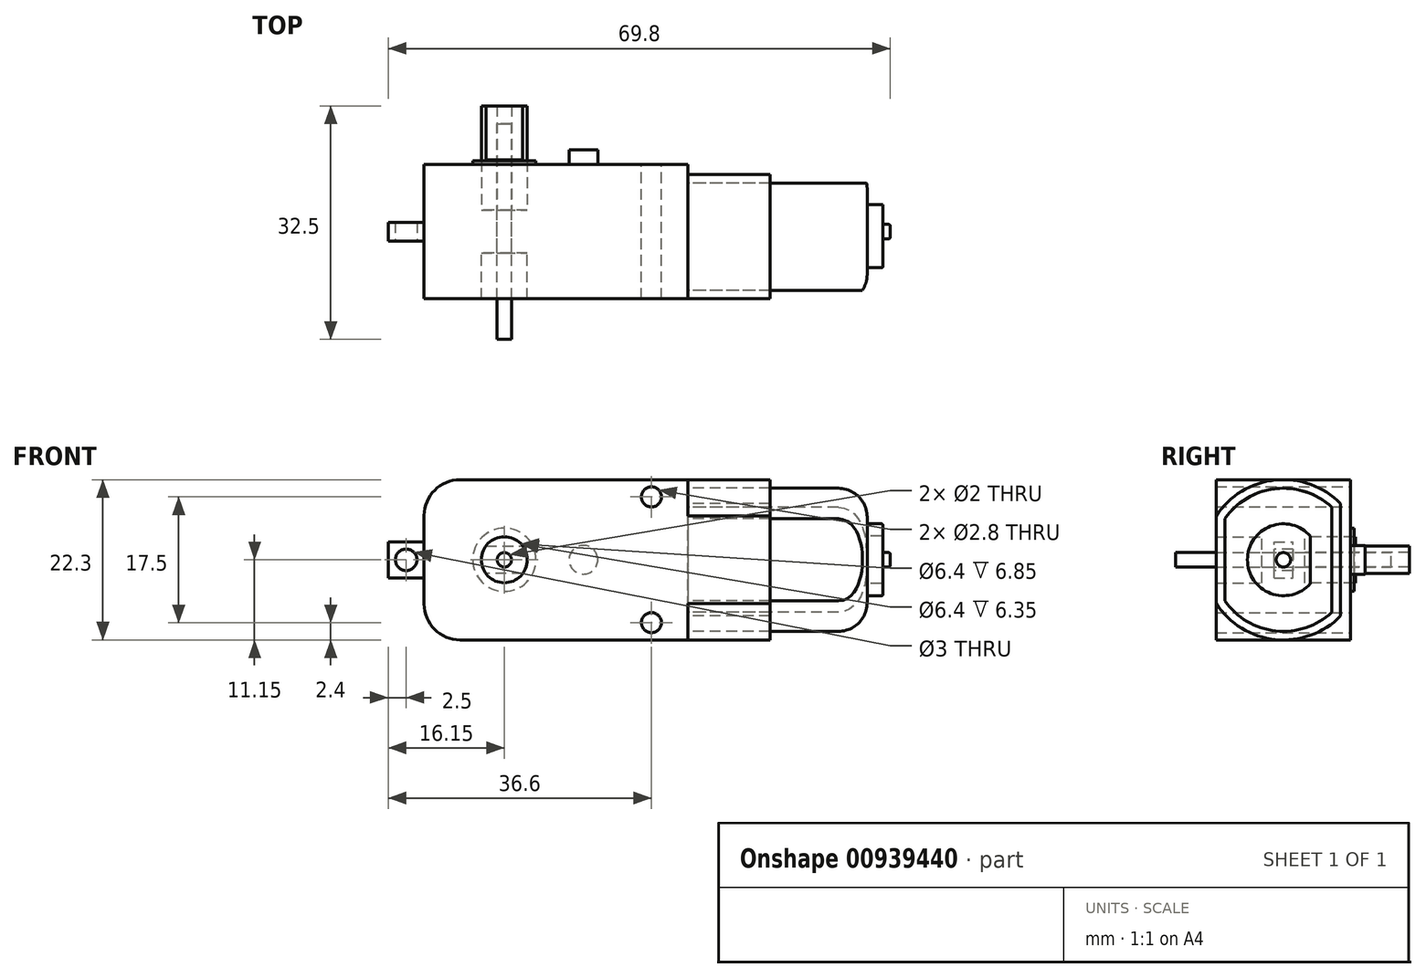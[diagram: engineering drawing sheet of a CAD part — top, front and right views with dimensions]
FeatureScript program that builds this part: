
annotation { "Feature Type Name" : "Feature", "Feature Type Description" : "" }
export const myFeature = defineFeature(function(context is Context, id is Id, definition is map)
    precondition{}
    {
        {
            var Q0;
            Q0=qCreatedBy(makeId("Front.planeOp"),FACE);
            var sketch = newSketch(context, id + "F0", { "sketchPlane" : qUnion([Q0])});
            skLineSegment(sketch, "E0.bottom", {"start": v(18.35, -11.15) * mm, "end": v(-13.35, -11.15) * mm});
            skLineSegment(sketch, "E0.top", {"start": v(18.35, 11.15) * mm, "end": v(-13.35, 11.15) * mm});
            skLineSegment(sketch, "E0.left", {"start": v(18.35, -11.15) * mm, "end": v(18.35, 11.15) * mm});
            skLineSegment(sketch, "E0.right", {"start": v(-18.35, -6.15) * mm, "end": v(-18.35, 6.15) * mm});
            skPoint(sketch, "E0.middle", {"position": v(0, 0) * mm});
            skPoint(sketch, "E1.visualSharp", {"position": v(-18.35, 11.15) * mm});
            skArc(sketch, "E1.filletArc", {"start": v(-13.35, 11.15) * mm, "mid": v(-16.89, 9.69) * mm, "end": v(-18.35, 6.15) * mm});
            skPoint(sketch, "E2.visualSharp", {"position": v(-18.35, -11.15) * mm});
            skArc(sketch, "E2.filletArc", {"start": v(-18.35, -6.15) * mm, "mid": v(-16.89, -9.69) * mm, "end": v(-13.35, -11.15) * mm});
            skLineSegment(sketch, "E3", {"start": v(-27.57, 10.15) * mm, "end": v(27, 10.15) * mm, "construction": true});
            skLineSegment(sketch, "E4", {"start": v(27, -10.15) * mm, "end": v(-33.16, -10.15) * mm, "construction": true});
            skLineSegment(sketch, "E5", {"start": v(14.65, 15.01) * mm, "end": v(14.65, -22.1) * mm, "construction": true});
            skCircle(sketch, "E6", {"center": v(13.25, 8.75) * mm, "radius": 1.4 * mm});
            skCircle(sketch, "E7.MirrorC", {"center": v(13.25, -8.75) * mm, "radius": 1.4 * mm});
            skCircle(sketch, "E8", {"center": v(-7.2, 0) * mm, "radius": 3.2 * mm});
            skCircle(sketch, "E9", {"center": v(-7.2, 0) * mm, "radius": 1 * mm});
            skCircle(sketch, "E10", {"center": v(3.8, 0) * mm, "radius": 2 * mm});
            skSolve(sketch);
        }
        {
            var Q0;
            Q0=makeQuery(id+"F0.imprint","IMPRINT",FACE,{"disambiguationData":[TD([[makeQuery(id+"F0.imprint","IMPRINT",EDGE,{"derivedFrom":sQuery(id+"F0.wireOp",EDGE,"E0.bottom")}),-1.0]])]});
            var Q1;
            Q1=makeQuery(id+"F0.imprint","IMPRINT",FACE,{"disambiguationData":[TD([[makeQuery(id+"F0.imprint","IMPRINT",EDGE,{"derivedFrom":sQuery(id+"F0.wireOp",EDGE,"E10")}),1.0]])]});
            extrude(context, id + "F1", {"entities" : qUnion([Q0, Q1]), "endBound" : BoundingType.SYMMETRIC, "offsetDistance" : 25 * mm, "depth" : (18.7) * mm});
        }
        {
            var Q0;
            Q0=makeQuery(id+"F0.imprint","IMPRINT",FACE,{"disambiguationData":[TD([[makeQuery(id+"F0.imprint","IMPRINT",EDGE,{"derivedFrom":sQuery(id+"F0.wireOp",EDGE,"E10")}),1.0]])]});
            var Q1;
            Q1=sQuery(id+"F0.wireOp",EDGE,"E10");
            extrude(context, id + "F2", {"entities" : qUnion([Q0]), "operationType" : NewBodyOperationType.ADD, "surfaceEntities" : qUnion([Q1]), "oppositeDirection" : true, "depth" : 11.35 * mm, "offsetDistance" : 25 * mm});
        }
        {
            var Q0;
            Q0=makeQuery(id+"F1.opExtrude","SWEPT_FACE",FACE,{"disambiguationData":[OSD([sQuery(id+"F0.wireOp",EDGE,"E0.right")])]});
            var sketch = newSketch(context, id + "F3", { "sketchPlane" : qUnion([Q0])});
            skLineSegment(sketch, "E11.bottom", {"start": v(1.3, -2.5) * mm, "end": v(-1.3, -2.5) * mm});
            skLineSegment(sketch, "E11.top", {"start": v(1.3, 2.5) * mm, "end": v(-1.3, 2.5) * mm});
            skLineSegment(sketch, "E11.left", {"start": v(1.3, -2.5) * mm, "end": v(1.3, 2.5) * mm});
            skLineSegment(sketch, "E11.right", {"start": v(-1.3, -2.5) * mm, "end": v(-1.3, 2.5) * mm});
            skPoint(sketch, "E11.middle", {"position": v(0, 0) * mm});
            skSolve(sketch);
        }
        {
            var Q0;
            Q0=makeQuery(id+"F3.imprint","IMPRINT",FACE,{"disambiguationData":[TD([[makeQuery(id+"F3.imprint","IMPRINT",EDGE,{"derivedFrom":sQuery(id+"F3.wireOp",EDGE,"E11.bottom")}),-1.0]])]});
            extrude(context, id + "F4", {"entities" : qUnion([Q0]), "operationType" : NewBodyOperationType.ADD, "depth" : 5 * mm});
        }
        {
            var Q0;
            Q0=makeQuery(id+"F4.opExtrude","SWEPT_FACE",FACE,{"disambiguationData":[OSD([sQuery(id+"F3.wireOp",EDGE,"E11.left")])]});
            var sketch = newSketch(context, id + "F5", { "sketchPlane" : qUnion([Q0])});
            skLineSegment(sketch, "E12", {"start": v(-23.35, 0) * mm, "end": v(-18.35, 0) * mm, "construction": true});
            skCircle(sketch, "E13", {"center": v(-20.85, 0) * mm, "radius": 1.5 * mm});
            skSolve(sketch);
        }
        {
            var Q0;
            Q0=makeQuery(id+"F5.imprint","IMPRINT",FACE,{"disambiguationData":[TD([[makeQuery(id+"F5.imprint","IMPRINT",EDGE,{"derivedFrom":sQuery(id+"F5.wireOp",EDGE,"E13")}),1.0]])]});
            extrude(context, id + "F6", {"entities" : qUnion([Q0]), "operationType" : NewBodyOperationType.REMOVE, "endBound" : BoundingType.THROUGH_ALL, "oppositeDirection" : true, "depth" : 25 * mm});
        }
        {
            var Q0;
            Q0=makeQuery(id+"F1.opExtrude","SWEPT_FACE",FACE,{"disambiguationData":[OSD([sQuery(id+"F0.wireOp",EDGE,"E0.left")])]});
            var sketch = newSketch(context, id + "F7", { "sketchPlane" : qUnion([Q0])});
            skArc(sketch, "E14", {"start": v(7.95, 7.82) * mm, "mid": v(-1.12, 11.1) * mm, "end": v(-9.35, 6.07) * mm});
            skLineSegment(sketch, "E15", {"start": v(7.95, 13.91) * mm, "end": v(7.95, -13.85) * mm, "construction": true});
            skLineSegment(sketch, "E16", {"start": v(-9.35, 11.15) * mm, "end": v(-9.35, -11.15) * mm, "construction": true});
            skArc(sketch, "E17.trimOffspring", {"start": v(-9.35, -6.07) * mm, "mid": v(-1.12, -11.1) * mm, "end": v(7.95, -7.82) * mm});
            skLineSegment(sketch, "E18", {"start": v(-9.35, 6.07) * mm, "end": v(-9.35, -6.07) * mm});
            skLineSegment(sketch, "E19", {"start": v(7.95, 7.82) * mm, "end": v(7.95, -7.82) * mm});
            skArc(sketch, "E20.0", {"start": v(-8.15, -5.7) * mm, "mid": v(-1.06, -9.9) * mm, "end": v(6.75, -7.31) * mm});
            skLineSegment(sketch, "E20.1", {"start": v(-8.15, 5.7) * mm, "end": v(-8.15, -5.7) * mm});
            skArc(sketch, "E20.2", {"start": v(6.75, 7.31) * mm, "mid": v(-1.06, 9.9) * mm, "end": v(-8.15, 5.7) * mm});
            skLineSegment(sketch, "E20.3", {"start": v(6.75, 7.31) * mm, "end": v(6.75, -7.31) * mm});
            skSolve(sketch);
        }
        {
            var Q0;
            {var subQ4=sQuery(id+"F7.wireOp",EDGE,"E18");Q0=makeQuery(id+"F7.imprint","IMPRINT",FACE,{"disambiguationData":[TD([[makeQuery(id+"F7.imprint","IMPRINT",EDGE,{"derivedFrom":subQ4}),-1.0]])]});}
            extrude(context, id + "F8", {"entities" : qUnion([Q0]), "operationType" : NewBodyOperationType.ADD, "depth" : 11.4 * mm});
        }
        {
            var Q0;
            Q0=makeQuery(id+"F8.boolean.opBoolean","SPLIT",FACE,{"disambiguationData":[TD([makeQuery(id+"F8.opExtrude","SWEPT_FACE",FACE,{"disambiguationData":[OSD([sQuery(id+"F7.wireOp",EDGE,"E20.0")])]}),makeQuery(id+"F8.opExtrude","SWEPT_FACE",FACE,{"disambiguationData":[OSD([sQuery(id+"F7.wireOp",EDGE,"E20.1")])]}),makeQuery(id+"F8.opExtrude","SWEPT_FACE",FACE,{"disambiguationData":[OSD([sQuery(id+"F7.wireOp",EDGE,"E20.2")])]}),makeQuery(id+"F8.opExtrude","SWEPT_FACE",FACE,{"disambiguationData":[OSD([sQuery(id+"F7.wireOp",EDGE,"E20.3")])]})])],"derivedFrom":makeQuery(id+"F1.opExtrude","SWEPT_FACE",FACE,{"disambiguationData":[OSD([sQuery(id+"F0.wireOp",EDGE,"E0.left")])]})});
            extrude(context, id + "F9", {"entities" : qUnion([Q0]), "depth" : (11.4 + 13.5) * mm});
        }
        {
            var Q0;
            Q0=makeQuery(id+"F9.opExtrude","CAP_EDGE",EDGE,{"disambiguationData":[OSD([sQuery(id+"F7.wireOp",EDGE,"E20.0")])],"isStart":false});
            fillet(context, id + "F10", {"entities" : qUnion([Q0]), "radius" : 4 * mm, "tangentPropagation" : true, "allowEdgeOverflow" : false});
        }
        {
            var Q0;
            Q0=makeQuery(id+"F9.opExtrude","CAP_FACE",FACE,{"disambiguationData":[OSD([sQuery(id+"F0.wireOp",EDGE,"E0.left")])],"isStart":false});
            var sketch = newSketch(context, id + "F11", { "sketchPlane" : qUnion([Q0])});
            skLineSegment(sketch, "E21", {"start": v(3.75, -5.9) * mm, "end": v(3.75, 7.54) * mm, "construction": true});
            skArc(sketch, "E22", {"start": v(3.75, 3.3) * mm, "mid": v(-5, 0) * mm, "end": v(3.75, -3.3) * mm});
            skLineSegment(sketch, "E23", {"start": v(3.75, 3.3) * mm, "end": v(3.75, -3.3) * mm});
            skCircle(sketch, "E24", {"center": v(0, 0) * mm, "radius": 1 * mm});
            skSolve(sketch);
        }
        {
            var Q0;
            Q0=makeQuery(id+"F0.imprint","IMPRINT",FACE,{"disambiguationData":[TD([[makeQuery(id+"F0.imprint","IMPRINT",EDGE,{"derivedFrom":sQuery(id+"F0.wireOp",EDGE,"E8")}),1.0]])]});
            extrude(context, id + "F12", {"entities" : qUnion([Q0]), "operationType" : NewBodyOperationType.ADD, "endBound" : BoundingType.SYMMETRIC, "depth" : 6 * mm});
        }
        {
            var Q0;
            Q0=makeQuery(id+"F0.imprint","IMPRINT",FACE,{"disambiguationData":[TD([[makeQuery(id+"F0.imprint","IMPRINT",EDGE,{"derivedFrom":sQuery(id+"F0.wireOp",EDGE,"E9")}),1.0]])]});
            extrude(context, id + "F13", {"entities" : qUnion([Q0]), "endBound" : BoundingType.SYMMETRIC, "depth" : 30 * mm});
        }
        {
            var Q0;
            Q0=makeQuery(id+"F1.opExtrude","CAP_FACE",FACE,{"disambiguationData":[OSD([sQuery(id+"F0.wireOp",EDGE,"E0.bottom"),sQuery(id+"F0.wireOp",EDGE,"E0.top"),sQuery(id+"F0.wireOp",EDGE,"E0.left"),sQuery(id+"F0.wireOp",EDGE,"E0.right"),sQuery(id+"F0.wireOp",EDGE,"E1.filletArc"),sQuery(id+"F0.wireOp",EDGE,"E2.filletArc"),sQuery(id+"F0.wireOp",EDGE,"E6"),sQuery(id+"F0.wireOp",EDGE,"E7.MirrorC"),sQuery(id+"F0.wireOp",EDGE,"E8")])],"isStart":true});
            var sketch = newSketch(context, id + "F14", { "sketchPlane" : qUnion([Q0])});
            skCircle(sketch, "E25", {"center": v(7.2, 0) * mm, "radius": 3.2 * mm});
            skCircle(sketch, "E26.0", {"center": v(7.2, 0) * mm, "radius": 4.4 * mm});
            skSolve(sketch);
        }
        {
            var Q0;
            Q0=makeQuery(id+"F14.imprint","IMPRINT",FACE,{"disambiguationData":[TD([[makeQuery(id+"F14.imprint","IMPRINT",EDGE,{"derivedFrom":sQuery(id+"F14.wireOp",EDGE,"E25")}),1.0]])]});
            extrude(context, id + "F15", {"entities" : qUnion([Q0]), "operationType" : NewBodyOperationType.ADD, "depth" : .5 * mm});
        }
        {
            var Q0;
            Q0=makeQuery(id+"F12.opExtrude","CAP_FACE",FACE,{"disambiguationData":[OSD([sQuery(id+"F0.wireOp",EDGE,"E8"),sQuery(id+"F0.wireOp",EDGE,"E9")])],"isStart":true});
            var sketch = newSketch(context, id + "F16", { "sketchPlane" : qUnion([Q0])});
            skCircle(sketch, "E27", {"center": v(7.2, 0) * mm, "radius": 1 * mm});
            skCircle(sketch, "E28", {"center": v(7.2, 0) * mm, "radius": 3.2 * mm});
            skSolve(sketch);
        }
        {
            var Q0;
            Q0=makeQuery(id+"F16.imprint","IMPRINT",FACE,{"disambiguationData":[TD([[makeQuery(id+"F16.imprint","IMPRINT",EDGE,{"derivedFrom":sQuery(id+"F16.wireOp",EDGE,"E27")}),1.0]])]});
            extrude(context, id + "F17", {"entities" : qUnion([Q0]), "depth" : 14.5 * mm});
        }
        {
            var Q0;
            Q0=makeQuery(id+"F17.opExtrude","CAP_FACE",FACE,{"disambiguationData":[OSD([sQuery(id+"F16.wireOp",EDGE,"E27"),sQuery(id+"F16.wireOp",EDGE,"E28")])],"isStart":false});
            var sketch = newSketch(context, id + "F18", { "sketchPlane" : qUnion([Q0])});
            skLineSegment(sketch, "E29", {"start": v(13.52, -1.92) * mm, "end": v(0.5, -1.92) * mm, "construction": true});
            skLineSegment(sketch, "E30", {"start": v(0.5, -1.92) * mm, "end": v(0.83, 1.03) * mm, "construction": true});
            skLineSegment(sketch, "E31.MirrorCS", {"start": v(13.52, 1.92) * mm, "end": v(0.5, 1.92) * mm, "construction": true});
            skLineSegment(sketch, "E32", {"start": v(9.76, 1.92) * mm, "end": v(4.64, 1.92) * mm});
            skLineSegment(sketch, "E33", {"start": v(4.64, -1.92) * mm, "end": v(9.76, -1.92) * mm});
            skSolve(sketch);
        }
        {
            var Q0;
            {var subQ0=sQuery(id+"F18.wireOp",EDGE,"E32");Q0=makeQuery(id+"F18.imprint","IMPRINT",FACE,{"disambiguationData":[TD([[makeQuery(id+"F18.imprint","IMPRINT",EDGE,{"derivedFrom":subQ0}),-1.0]])]});}
            var Q1;
            {var subQ0=sQuery(id+"F18.wireOp",EDGE,"E33");Q1=makeQuery(id+"F18.imprint","IMPRINT",FACE,{"disambiguationData":[TD([[makeQuery(id+"F18.imprint","IMPRINT",EDGE,{"derivedFrom":subQ0}),-1.0]])]});}
            extrude(context, id + "F19", {"entities" : qUnion([Q0, Q1]), "operationType" : NewBodyOperationType.REMOVE, "oppositeDirection" : true, "depth" : 7.5 * mm});
        }
        {
            var Q0;
            Q0=makeQuery(id+"F11.imprint","IMPRINT",FACE,{"disambiguationData":[TD([[makeQuery(id+"F11.imprint","IMPRINT",EDGE,{"derivedFrom":sQuery(id+"F11.wireOp",EDGE,"E22")}),1.0]])]});
            extrude(context, id + "F20", {"entities" : qUnion([Q0]), "operationType" : NewBodyOperationType.ADD, "depth" : 2.2 * mm});
        }
        {
            var Q0;
            Q0=makeQuery(id+"F11.imprint","IMPRINT",FACE,{"disambiguationData":[TD([[makeQuery(id+"F11.imprint","IMPRINT",EDGE,{"derivedFrom":sQuery(id+"F11.wireOp",EDGE,"E24")}),1.0]])]});
            extrude(context, id + "F21", {"entities" : qUnion([Q0]), "operationType" : NewBodyOperationType.ADD, "depth" : 3.2 * mm});
        }
        {
            var Q0;
            Q0=makeQuery(id+"F20.opExtrude","CAP_EDGE",EDGE,{"disambiguationData":[OSD([sQuery(id+"F11.wireOp",EDGE,"E22")])],"isStart":false});
            var Q1;
            Q1=makeQuery(id+"F21.opExtrude","CAP_EDGE",EDGE,{"disambiguationData":[OSD([sQuery(id+"F11.wireOp",EDGE,"E24")])],"isStart":false});
            fillet(context, id + "F22", {"entities" : qUnion([Q0, Q1]), "radius" : .2 * mm, "tangentPropagation" : true, "allowEdgeOverflow" : false});
        }
    });
